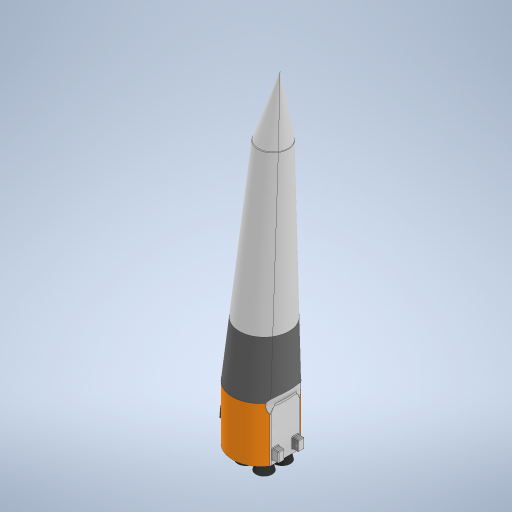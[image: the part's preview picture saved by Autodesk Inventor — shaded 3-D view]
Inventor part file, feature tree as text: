
AUTODESK INVENTOR PART (.ipt)
format: ipt  version: 2023 (Build 270158030, 158C)  size: 888,832 bytes
history: native  units: mm
features: other x4, split x1, sketch x1
ambient origin geometry x8: Origin, YZ Plane, XZ Plane, XY Plane, X Axis, Y Axis, Z Axis, Center Point
bodies: Solid2 (feature_tree), Solid3 (feature_tree)
feature tree (6):
  other  "Soyuz Model.ipt"
  split  "Split1"
  other  "Soyuz Booster::Soyuz Model.ipt"
  other  "TaggingFeature1"
  sketch  "Sketch1"  dims[d0=10.0mm d1=55.0mm]
  other  "Soyuz Booster"
